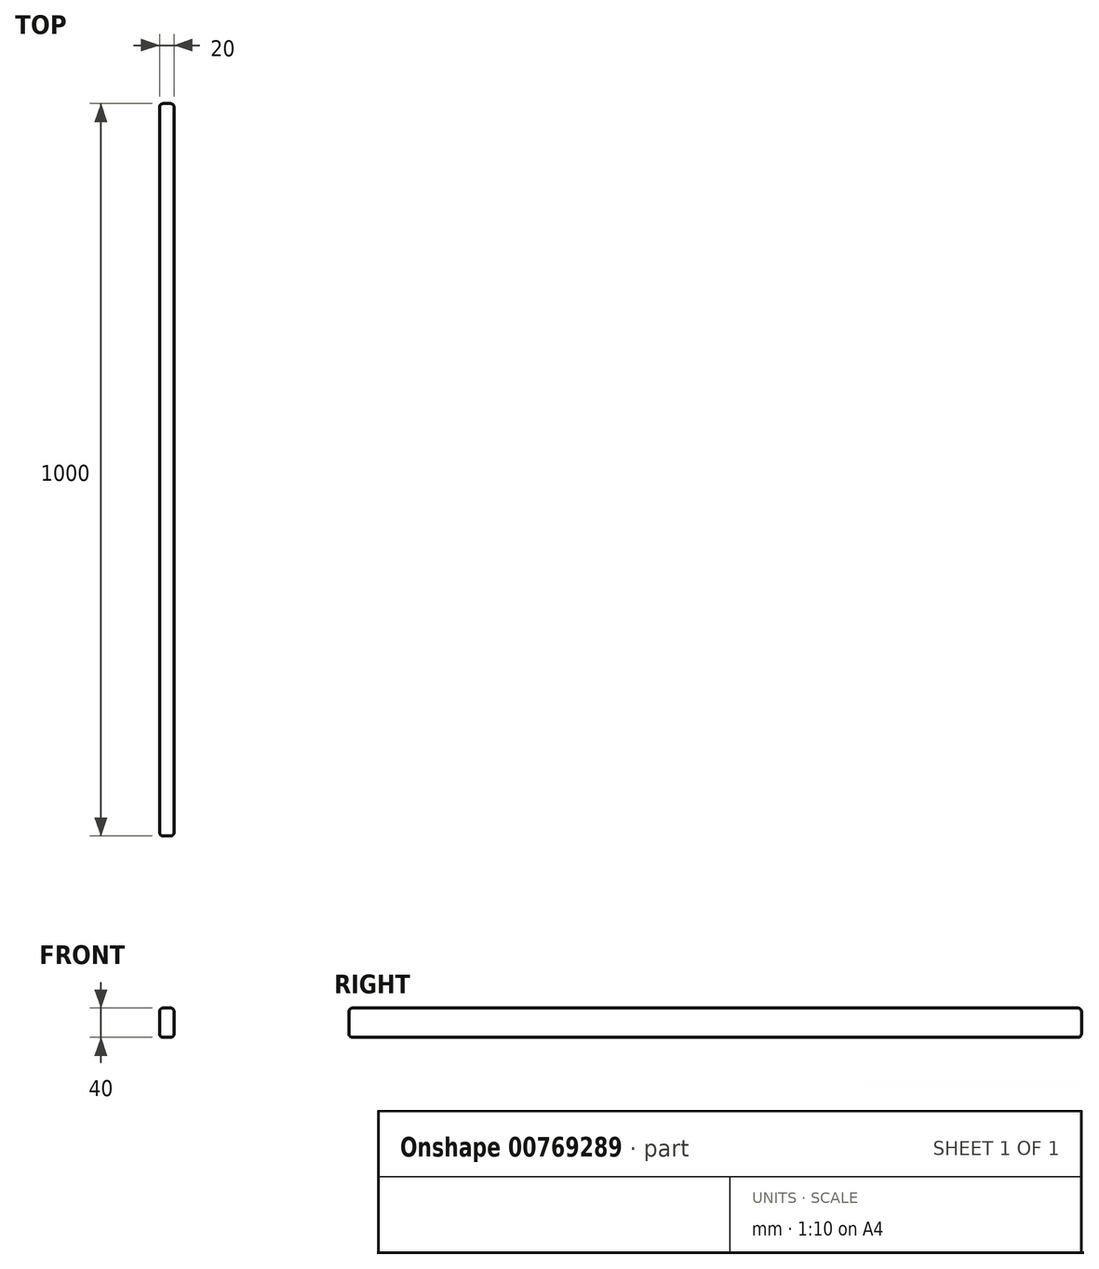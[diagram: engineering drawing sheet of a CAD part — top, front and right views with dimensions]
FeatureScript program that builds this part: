
annotation { "Feature Type Name" : "Feature", "Feature Type Description" : "" }
export const myFeature = defineFeature(function(context is Context, id is Id, definition is map)
    precondition{}
    {
        {
            var Q0;
            Q0=qCreatedBy(makeId("Top.planeOp"),FACE);
            var sketch = newSketch(context, id + "F0", { "sketchPlane" : qUnion([Q0])});
            skLineSegment(sketch, "E0.bottom", {"start": v(0, 0) * mm, "end": v(20, 0) * mm});
            skLineSegment(sketch, "E0.top", {"start": v(0, 1000) * mm, "end": v(20, 1000) * mm});
            skLineSegment(sketch, "E0.left", {"start": v(0, 0) * mm, "end": v(0, 1000) * mm});
            skLineSegment(sketch, "E0.right", {"start": v(20, 0) * mm, "end": v(20, 1000) * mm});
            skSolve(sketch);
        }
        {
            var Q0;
            Q0=makeQuery(id+"F0.imprint","IMPRINT",FACE,{"disambiguationData":[TD([[makeQuery(id+"F0.imprint","IMPRINT",EDGE,{"derivedFrom":sQuery(id+"F0.wireOp",EDGE,"E0.bottom")}),1.0]])]});
            extrude(context, id + "F1", {"entities" : qUnion([Q0]), "depth" : 40 * mm, "offsetDistance" : 25 * mm});
        }
        {
            var Q0;
            Q0=makeQuery(id+"F1.opExtrude","CAP_EDGE",EDGE,{"disambiguationData":[OSD([sQuery(id+"F0.wireOp",EDGE,"E0.left")])],"isStart":false});
            var Q1;
            Q1=makeQuery(id+"F1.opExtrude","CAP_EDGE",EDGE,{"disambiguationData":[OSD([sQuery(id+"F0.wireOp",EDGE,"E0.right")])],"isStart":false});
            var Q2;
            Q2=makeQuery(id+"F1.opExtrude","CAP_EDGE",EDGE,{"disambiguationData":[OSD([sQuery(id+"F0.wireOp",EDGE,"E0.left")])],"isStart":true});
            var Q3;
            Q3=makeQuery(id+"F1.opExtrude","CAP_EDGE",EDGE,{"disambiguationData":[OSD([sQuery(id+"F0.wireOp",EDGE,"E0.right")])],"isStart":true});
            var Q4;
            Q4=makeQuery(id+"F1.opExtrude","SWEPT_EDGE",EDGE,{"disambiguationData":[OSD([sQuery(id+"F0.wireOp",EDGE,"E0.bottom"),sQuery(id+"F0.wireOp",EDGE,"E0.left")])]});
            var Q5;
            Q5=makeQuery(id+"F1.opExtrude","SWEPT_EDGE",EDGE,{"disambiguationData":[OSD([sQuery(id+"F0.wireOp",EDGE,"E0.bottom"),sQuery(id+"F0.wireOp",EDGE,"E0.right")])]});
            var Q6;
            Q6=makeQuery(id+"F1.opExtrude","CAP_EDGE",EDGE,{"disambiguationData":[OSD([sQuery(id+"F0.wireOp",EDGE,"E0.bottom")])],"isStart":false});
            var Q7;
            Q7=makeQuery(id+"F1.opExtrude","CAP_EDGE",EDGE,{"disambiguationData":[OSD([sQuery(id+"F0.wireOp",EDGE,"E0.bottom")])],"isStart":true});
            var Q8;
            Q8=makeQuery(id+"F1.opExtrude","SWEPT_EDGE",EDGE,{"disambiguationData":[OSD([sQuery(id+"F0.wireOp",EDGE,"E0.top"),sQuery(id+"F0.wireOp",EDGE,"E0.right")])]});
            var Q9;
            Q9=makeQuery(id+"F1.opExtrude","CAP_EDGE",EDGE,{"disambiguationData":[OSD([sQuery(id+"F0.wireOp",EDGE,"E0.top")])],"isStart":false});
            var Q10;
            Q10=makeQuery(id+"F1.opExtrude","SWEPT_EDGE",EDGE,{"disambiguationData":[OSD([sQuery(id+"F0.wireOp",EDGE,"E0.top"),sQuery(id+"F0.wireOp",EDGE,"E0.left")])]});
            var Q11;
            Q11=makeQuery(id+"F1.opExtrude","CAP_EDGE",EDGE,{"disambiguationData":[OSD([sQuery(id+"F0.wireOp",EDGE,"E0.top")])],"isStart":true});
            fillet(context, id + "F2", {"entities" : qUnion([Q0, Q1, Q2, Q3, Q4, Q5, Q6, Q7, Q8, Q9, Q10, Q11]), "radius" : 5 * mm, "tangentPropagation" : true, "allowEdgeOverflow" : false});
        }
    });
